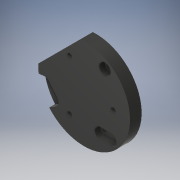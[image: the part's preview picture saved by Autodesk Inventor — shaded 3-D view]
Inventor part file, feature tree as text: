
AUTODESK INVENTOR PART (.ipt)
format: ipt  version: 2018 (Build 220112000, 112)  size: 220,672 bytes
history: native  units: in
note: dims shown in document units (in); Inventor stores cm internally (conversion verified against a paired STEP export)
features: extrude x12, sketch x8, thread x3
ambient origin geometry x8: Origin, YZ Plane, XZ Plane, XY Plane, X Axis, Y Axis, Z Axis, Center Point
bodies: Solid1 (feature_tree)
feature tree (23):
  extrude  "Extrusion1"  Depth=0.2362in
  sketch  "Sketch2"  dims[d9=0.2362in d10=0.2362in]
  extrude  "Extrusion2"  Depth=0.2362in
  extrude  "Extrusion3"  Depth=0.3937in
  extrude  "Extrusion4"  Depth=0.3937in
  sketch  "Sketch3"  dims[d11=0.3937in d12=0.0in d13=0.3937in]
  extrude  "Extrusion5"  Depth=0.1969in TaperAngle=0.0deg
  extrude  "Extrusion6"  Depth=0.1969in
  extrude  "Extrusion7"  Depth=0.3937in TaperAngle=0.0deg
  sketch  "Sketch5"  dims[d14=0.3937in d15=0.3937in]
  extrude  "Extrusion11"  Depth=0.3937in TaperAngle=0.0deg
  sketch  "Sketch6"  dims[d16=0.1969in d17=0.0in d18=0.1969in d19=0.0in]
  extrude  "Extrusion14"  Depth=0.3937in
  extrude  "Extrusion15"  Depth=0.1969in TaperAngle=0.0deg
  extrude  "Extrusion16"  Depth=0.3937in
  extrude  "Extrusion17"  Depth=0.3937in
  thread  "Thread1"  [1 undecoded]
  thread  "Thread2"  [1 undecoded]
  thread  "Thread3"  [1 undecoded]
  sketch  "Sketch1"  dims[d0=3.0906in d6=0.2362in]
  sketch  "Sketch7"  dims[d20=0.1969in d21=0.0in d24=0.1575in]
  sketch  "Sketch8"  dims[d25=1.1811in d27=360.0deg d29=0.3937in d30=0.0in]
  sketch  "Sketch9"  dims[d31=0.3937in d32=0.0in d33=0.3937in d34=0.0in d57=0.3937in d62=0.1969in d63=0.0in d69=4.1732in d70=0.2362in d71=0.2362in d74=0.1969in d75=0.0in d77=135.0deg d78=0.3937in d79=0.0in d84=0.3937in d87=0.3937in d88=0.1969in d89=0.0in d90=0.2362in d92=0.2362in d93=0.1969in d94=0.0in d95=0.3937in d96=0.0in d97=0.3937in d98=0.0in d99=0.3937in d100=0.0in]
note: 3 required parameter values undecoded (feature->parameter linkage not recoverable at this tier; creation-order binding heuristic only, values carry confidence <= 0.55)
